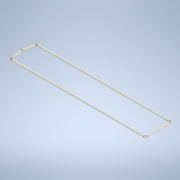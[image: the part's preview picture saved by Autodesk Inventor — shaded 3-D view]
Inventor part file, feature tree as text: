
AUTODESK INVENTOR PART (.ipt)
format: ipt  version: 2021 (Build 250183000, 183)  size: 139,776 bytes
history: native  units: in
note: dims shown in document units (in); Inventor stores cm internally (conversion verified against a paired STEP export)
features: plane x1, sweep x1, sketch x1
ambient origin geometry x8: Origin, YZ Plane, XZ Plane, XY Plane, X Axis, Y Axis, Z Axis, Center Point
bodies: Solid1 (feature_tree)
feature tree (3):
  plane  "Work Plane2"
  sweep  "Sweep1"
  sketch  "Sketch3"  dims[d23=0.375in d24=0.0in d25=0.0in d26=30.0in d27=5.75in d28=0.0in d29=0.0in d30=0.0in d31=0.0in d32=30.0in d34=0.5497in d35=0.125in d36=0.25in]
